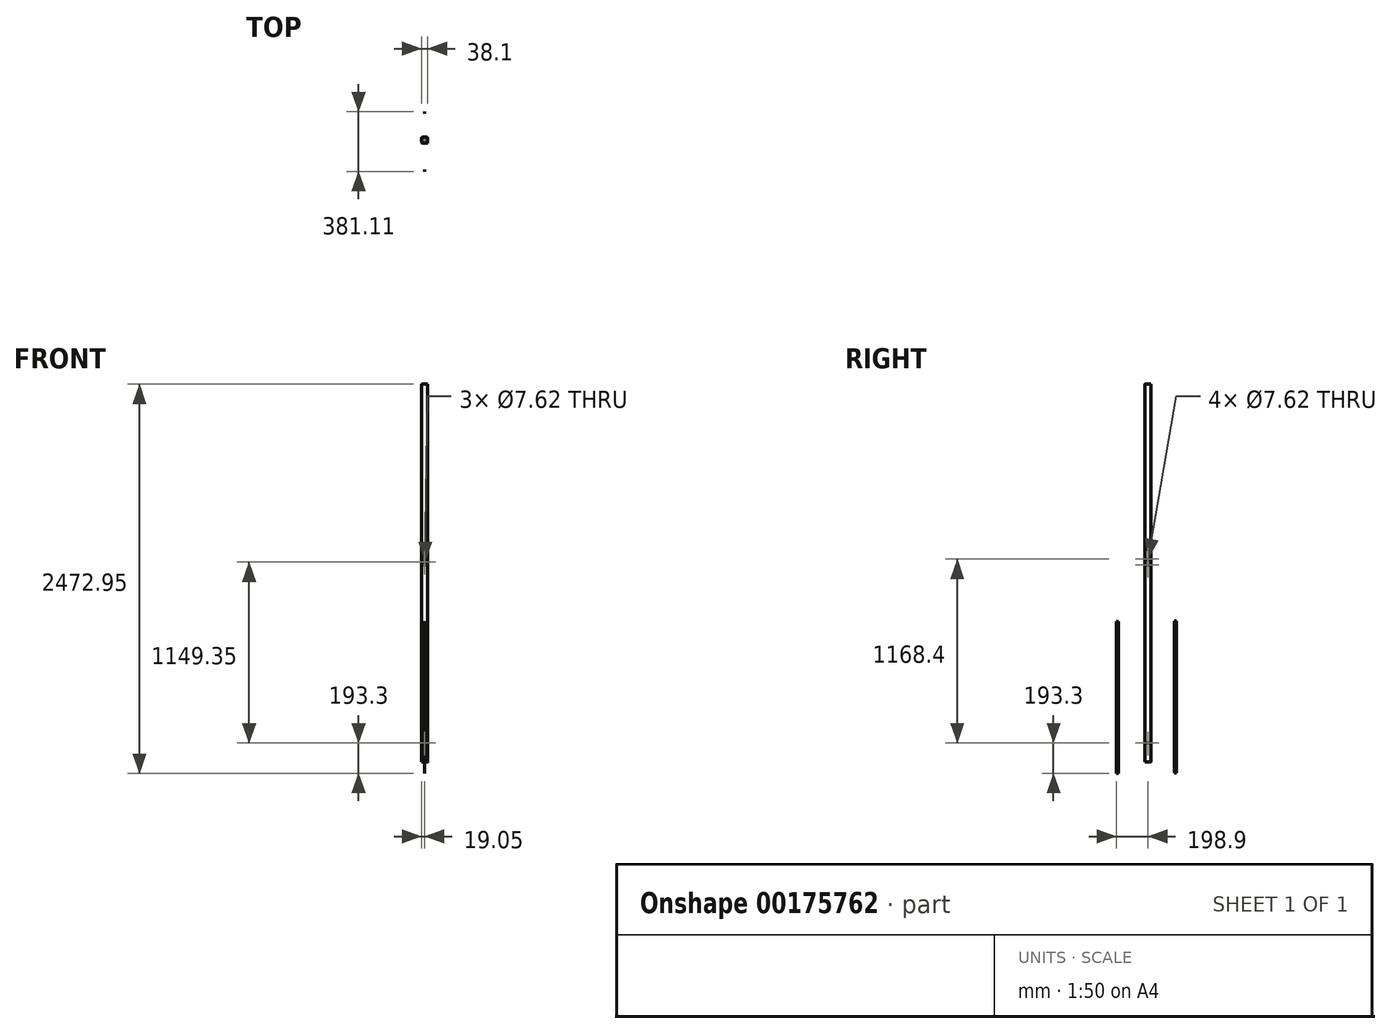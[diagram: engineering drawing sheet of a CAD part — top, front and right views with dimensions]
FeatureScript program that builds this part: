
annotation { "Feature Type Name" : "Feature", "Feature Type Description" : "" }
export const myFeature = defineFeature(function(context is Context, id is Id, definition is map)
    precondition{}
    {
        {
            var Q0;
            Q0=qCreatedBy(makeId("Top.planeOp"),FACE);
            var sketch = newSketch(context, id + "F0", { "sketchPlane" : qUnion([Q0])});
            skLineSegment(sketch, "E0.bottom", {"start": v(12.7, 19.05) * mm, "end": v(-12.7, 19.05) * mm});
            skLineSegment(sketch, "E0.top", {"start": v(12.7, -19.05) * mm, "end": v(-12.7, -19.05) * mm});
            skLineSegment(sketch, "E0.left", {"start": v(19.05, 12.7) * mm, "end": v(19.05, -12.7) * mm});
            skLineSegment(sketch, "E0.right", {"start": v(-19.05, 12.7) * mm, "end": v(-19.05, -12.7) * mm});
            skPoint(sketch, "E0.middle", {"position": v(0, 0) * mm});
            skPoint(sketch, "E1.visualSharp", {"position": v(-19.05, 19.05) * mm});
            skArc(sketch, "E1.filletArc", {"start": v(-12.7, 19.05) * mm, "mid": v(-17.2, 17.2) * mm, "end": v(-19.05, 12.7) * mm});
            skPoint(sketch, "E2.visualSharp", {"position": v(19.05, 19.05) * mm});
            skArc(sketch, "E2.filletArc", {"start": v(19.05, 12.7) * mm, "mid": v(17.2, 17.2) * mm, "end": v(12.7, 19.05) * mm});
            skPoint(sketch, "E3.visualSharp", {"position": v(19.05, -19.05) * mm});
            skArc(sketch, "E3.filletArc", {"start": v(12.7, -19.05) * mm, "mid": v(17.2, -17.2) * mm, "end": v(19.05, -12.7) * mm});
            skPoint(sketch, "E4.visualSharp", {"position": v(-19.05, -19.05) * mm});
            skArc(sketch, "E4.filletArc", {"start": v(-19.05, -12.7) * mm, "mid": v(-17.2, -17.2) * mm, "end": v(-12.7, -19.05) * mm});
            skSolve(sketch);
        }
        {
            var Q0;
            Q0=qSketchRegion(id+"F0",true);
            extrude(context, id + "F1", {"entities" : qUnion([Q0]), "depth" : 2400.3 * mm});
        }
        {
            var Q0;
            Q0=qCreatedBy(makeId("Right.planeOp"),FACE);
            var sketch = newSketch(context, id + "F2", { "sketchPlane" : qUnion([Q0])});
            skLineSegment(sketch, "E5.bottom", {"start": v(-186.2, -72.65) * mm, "end": v(-198.9, -72.65) * mm});
            skLineSegment(sketch, "E5.top", {"start": v(-186.2, 892.55) * mm, "end": v(-198.9, 892.55) * mm});
            skLineSegment(sketch, "E5.left", {"start": v(-186.2, -72.65) * mm, "end": v(-186.2, 892.55) * mm});
            skLineSegment(sketch, "E5.right", {"start": v(-198.9, -72.65) * mm, "end": v(-198.9, 892.55) * mm});
            skPoint(sketch, "E5.middle", {"position": v(-192.55, 409.95) * mm});
            skSolve(sketch);
        }
        {
            var Q0;
            Q0=qCreatedBy(makeId("Right.planeOp"),FACE);
            var sketch = newSketch(context, id + "F3", { "sketchPlane" : qUnion([Q0])});
            skLineSegment(sketch, "E6.bottom", {"start": v(182.21, -70.47) * mm, "end": v(169.51, -70.47) * mm});
            skLineSegment(sketch, "E6.top", {"start": v(182.21, 894.73) * mm, "end": v(169.51, 894.73) * mm});
            skLineSegment(sketch, "E6.left", {"start": v(182.21, -70.47) * mm, "end": v(182.21, 894.73) * mm});
            skLineSegment(sketch, "E6.right", {"start": v(169.51, -70.47) * mm, "end": v(169.51, 894.73) * mm});
            skPoint(sketch, "E6.middle", {"position": v(175.86, 412.13) * mm});
            skSolve(sketch);
        }
        {
            var Q0;
            Q0=makeQuery(id+"F2.imprint","IMPRINT",FACE,{"disambiguationData":[TD([[makeQuery(id+"F2.imprint","IMPRINT",EDGE,{"derivedFrom":sQuery(id+"F2.wireOp",EDGE,"E5.bottom")}),-1.0]])]});
            extrude(context, id + "F4", {"entities" : qUnion([Q0]), "depth" : 0.25 * mm});
        }
        {
            var Q0;
            Q0=makeQuery(id+"F3.imprint","IMPRINT",FACE,{"disambiguationData":[TD([[makeQuery(id+"F3.imprint","IMPRINT",EDGE,{"derivedFrom":sQuery(id+"F3.wireOp",EDGE,"E6.bottom")}),-1.0]])]});
            extrude(context, id + "F5", {"entities" : qUnion([Q0]), "depth" : 0.25 * mm});
        }
        {
            var Q0;
            Q0=makeQuery(id+"F1.opExtrude","SWEPT_FACE",FACE,{"disambiguationData":[OSD([sQuery(id+"F0.wireOp",EDGE,"E0.top")])]});
            var sketch = newSketch(context, id + "F6", { "sketchPlane" : qUnion([Q0])});
            skLineSegment(sketch, "E7", {"start": v(0, 0) * mm, "end": v(0, 120.65) * mm});
            skPoint(sketch, "E7.endSnap0", {"position": v(0, 0) * mm});
            skCircle(sketch, "E8", {"center": v(0, 120.65) * mm, "radius": 3.81 * mm});
            skSolve(sketch);
        }
        {
            var Q0;
            Q0 = qSketchRegion(id + "F6", true);
            extrude(context, id + "F7", {"entities" : qUnion([Q0]), "operationType" : NewBodyOperationType.REMOVE, "oppositeDirection" : true, "depth" : 38.1 * mm});
        }
        {
            var Q0;
            Q0=makeQuery(id+"F1.opExtrude","SWEPT_FACE",FACE,{"disambiguationData":[OSD([sQuery(id+"F0.wireOp",EDGE,"E0.left")])]});
            var sketch = newSketch(context, id + "F8", { "sketchPlane" : qUnion([Q0])});
            skLineSegment(sketch, "E9", {"start": v(0, 0) * mm, "end": v(0, 120.65) * mm});
            skCircle(sketch, "E10", {"center": v(0, 120.65) * mm, "radius": 3.81 * mm});
            skSolve(sketch);
        }
        {
            var Q0;
            Q0 = qSketchRegion(id + "F8", true);
            extrude(context, id + "F9", {"entities" : qUnion([Q0]), "operationType" : NewBodyOperationType.REMOVE, "oppositeDirection" : true, "depth" : 38.1 * mm});
        }
        {
            var Q0;
            Q0=makeQuery(id+"F1.opExtrude","SWEPT_FACE",FACE,{"disambiguationData":[OSD([sQuery(id+"F0.wireOp",EDGE,"E0.left")])]});
            var sketch = newSketch(context, id + "F10", { "sketchPlane" : qUnion([Q0])});
            skLineSegment(sketch, "E11", {"start": v(0, 2400.3) * mm, "end": v(0, 1289.05) * mm});
            skCircle(sketch, "E12", {"center": v(0, 1289.05) * mm, "radius": 3.81 * mm});
            skLineSegment(sketch, "E13", {"start": v(0, 1289.05) * mm, "end": v(0, 1250.95) * mm});
            skCircle(sketch, "E14", {"center": v(0, 1250.95) * mm, "radius": 3.8 * mm});
            skSolve(sketch);
        }
        {
            var Q0;
            Q0 = qSketchRegion(id + "F10", true);
            extrude(context, id + "F11", {"entities" : qUnion([Q0]), "operationType" : NewBodyOperationType.REMOVE, "oppositeDirection" : true, "depth" : 38.1 * mm});
        }
        {
            var Q0;
            Q0=makeQuery(id+"F1.opExtrude","SWEPT_FACE",FACE,{"disambiguationData":[OSD([sQuery(id+"F0.wireOp",EDGE,"E0.top")])]});
            var sketch = newSketch(context, id + "F12", { "sketchPlane" : qUnion([Q0])});
            skLineSegment(sketch, "E15", {"start": v(0, 2400.3) * mm, "end": v(0, 1270) * mm});
            skPoint(sketch, "E15.endSnap0", {"position": v(0, 2400.3) * mm});
            skCircle(sketch, "E16", {"center": v(0, 1270) * mm, "radius": 3.81 * mm});
            skSolve(sketch);
        }
        {
            var Q0;
            Q0 = qSketchRegion(id + "F12", true);
            extrude(context, id + "F13", {"entities" : qUnion([Q0]), "operationType" : NewBodyOperationType.REMOVE, "oppositeDirection" : true, "depth" : 38.1 * mm});
        }
    });
